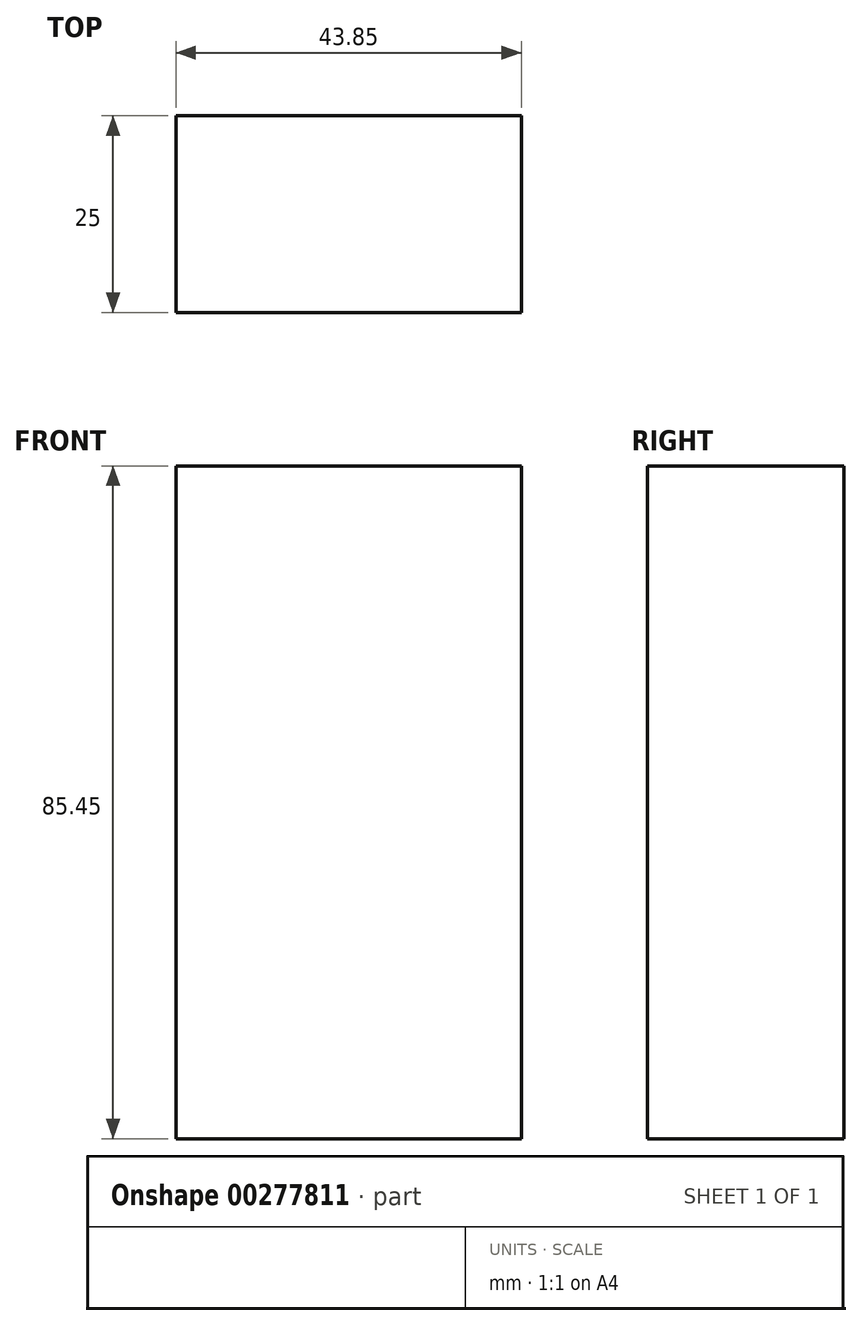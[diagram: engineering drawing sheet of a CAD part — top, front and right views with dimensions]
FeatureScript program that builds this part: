
annotation { "Feature Type Name" : "Feature", "Feature Type Description" : "" }
export const myFeature = defineFeature(function(context is Context, id is Id, definition is map)
    precondition{}
    {
        {
            var Q0;
            Q0=qCreatedBy(makeId("Front.planeOp"),FACE);
            var sketch = newSketch(context, id + "F0", { "sketchPlane" : qUnion([Q0])});
            skLineSegment(sketch, "E0.bottom", {"start": v(-86.85, 11.52) * mm, "end": v(-43, 11.52) * mm});
            skLineSegment(sketch, "E0.top", {"start": v(-86.85, 96.97) * mm, "end": v(-43, 96.97) * mm});
            skLineSegment(sketch, "E0.left", {"start": v(-86.85, 11.52) * mm, "end": v(-86.85, 96.97) * mm});
            skLineSegment(sketch, "E0.right", {"start": v(-43, 11.52) * mm, "end": v(-43, 96.97) * mm});
            skPoint(sketch, "E0.middle", {"position": v(-64.93, 54.25) * mm});
            skSolve(sketch);
        }
        {
            var Q0;
            Q0=makeQuery(id+"F0.imprint","IMPRINT",FACE,{"disambiguationData":[TD([[makeQuery(id+"F0.imprint","IMPRINT",EDGE,{"derivedFrom":sQuery(id+"F0.wireOp",EDGE,"E0.bottom")}),1.0]])]});
            extrude(context, id + "F1", {"entities" : qUnion([Q0]), "depth" : 25 * mm});
        }
    });
